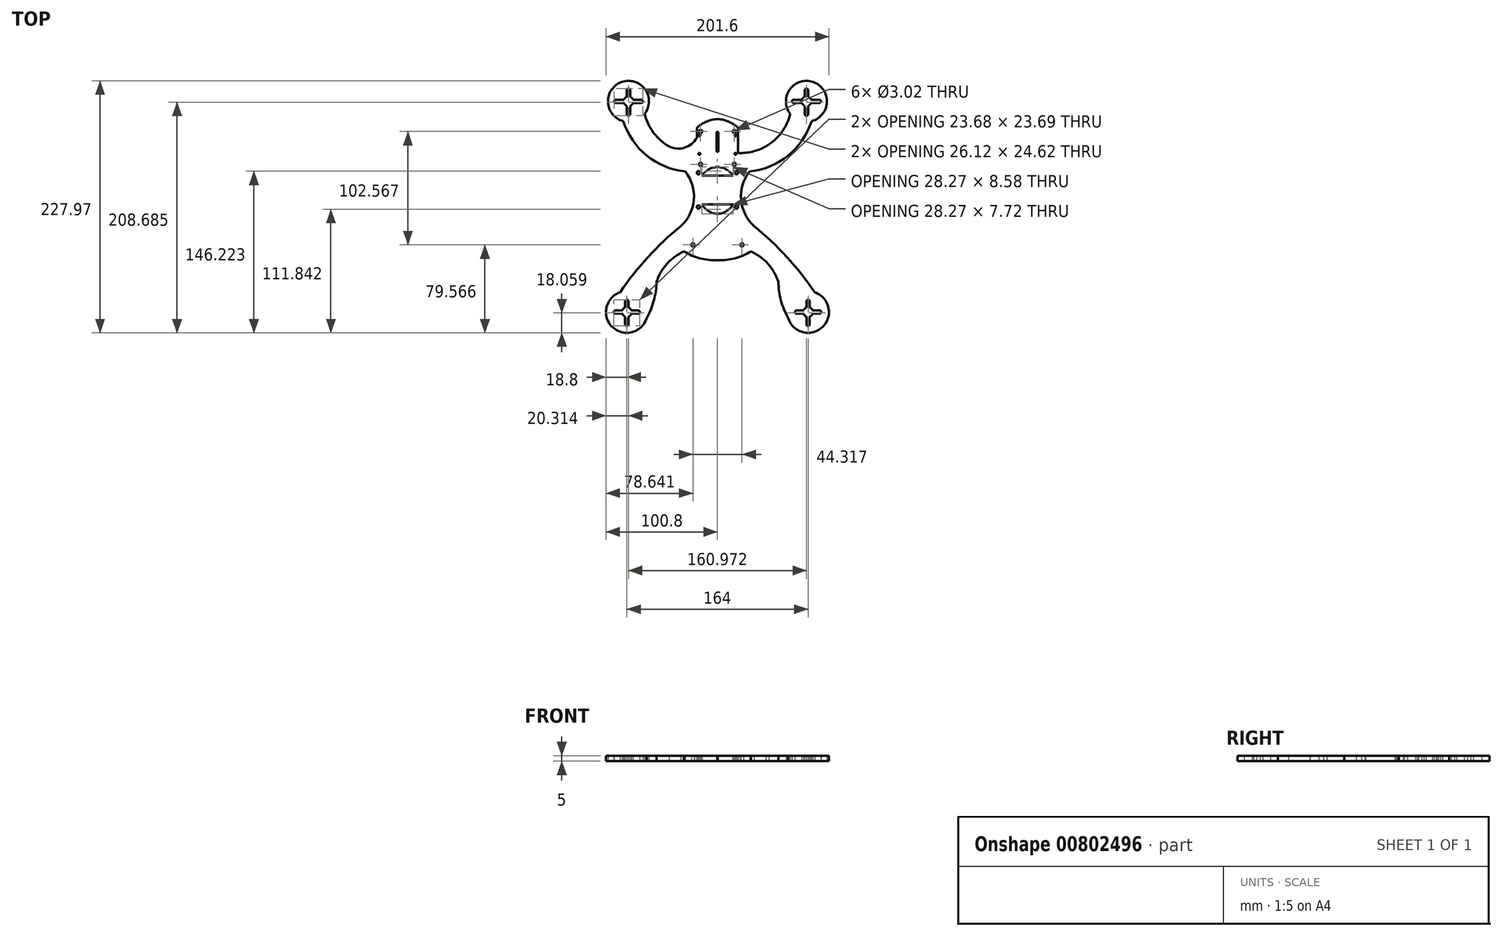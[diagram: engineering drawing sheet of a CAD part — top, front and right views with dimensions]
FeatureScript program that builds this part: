
annotation { "Feature Type Name" : "Feature", "Feature Type Description" : "" }
export const myFeature = defineFeature(function(context is Context, id is Id, definition is map)
    precondition{}
    {
        {
            var Q0;
            Q0=qCreatedBy(makeId("Top.planeOp"),FACE);
            var sketch = newSketch(context, id + "F0", { "sketchPlane" : qUnion([Q0])});
            skLineSegment(sketch, "E0", {"start": v(0, 59.62) * mm, "end": v(0, -52.38) * mm});
            skLineSegment(sketch, "E1", {"start": v(0, -52.38) * mm, "end": v(-30.19, -52.38) * mm});
            skCircle(sketch, "E2", {"center": v(-82, -107.2) * mm, "radius": 18.8 * mm});
            skCircle(sketch, "E3", {"center": v(-82, -107.2) * mm, "radius": 4.36 * mm});
            skCircle(sketch, "E4", {"center": v(-82, -118.3) * mm, "radius": 1.5 * mm});
            skCircle(sketch, "E5", {"center": v(-82, -97.6) * mm, "radius": 1.5 * mm});
            skCircle(sketch, "E6", {"center": v(-71.66, -107.2) * mm, "radius": 1.5 * mm});
            skCircle(sketch, "E7", {"center": v(-92.34, -107.2) * mm, "radius": 1.5 * mm});
            skLineSegment(sketch, "E8", {"start": v(-92.34, -108.7) * mm, "end": v(-86.1, -108.7) * mm});
            skLineSegment(sketch, "E9", {"start": v(-71.66, -108.7) * mm, "end": v(-77.9, -108.7) * mm});
            skLineSegment(sketch, "E10", {"start": v(-71.66, -105.7) * mm, "end": v(-77.9, -105.7) * mm});
            skLineSegment(sketch, "E11", {"start": v(-83.5, -118.3) * mm, "end": v(-83.5, -111.3) * mm});
            skLineSegment(sketch, "E12", {"start": v(-80.5, -118.3) * mm, "end": v(-80.5, -111.3) * mm});
            skLineSegment(sketch, "E13", {"start": v(-80.5, -97.6) * mm, "end": v(-80.5, -103.11) * mm});
            skLineSegment(sketch, "E14", {"start": v(-83.5, -97.6) * mm, "end": v(-83.5, -103.11) * mm});
            skCircle(sketch, "E15", {"center": v(-80.49, 83.43) * mm, "radius": 18.53 * mm});
            skArc(sketch, "E16", {"start": v(-64, -112.66) * mm, "mid": v(-57.49, -96.8) * mm, "end": v(-55.08, -79.81) * mm});
            skCircle(sketch, "E17", {"center": v(-80.49, 83.43) * mm, "radius": 4.36 * mm});
            skCircle(sketch, "E18", {"center": v(-80.49, 71.87) * mm, "radius": 1.5 * mm});
            skCircle(sketch, "E19", {"center": v(-68.93, 83.43) * mm, "radius": 1.5 * mm});
            skCircle(sketch, "E20", {"center": v(-92.05, 83.43) * mm, "radius": 1.5 * mm});
            skCircle(sketch, "E21", {"center": v(-80.49, 93.49) * mm, "radius": 1.5 * mm});
            skLineSegment(sketch, "E22", {"start": v(-92.05, 84.93) * mm, "end": v(-84.58, 84.93) * mm});
            skLineSegment(sketch, "E23", {"start": v(-92.05, 81.93) * mm, "end": v(-84.58, 81.93) * mm});
            skLineSegment(sketch, "E24", {"start": v(-78.99, 71.87) * mm, "end": v(-78.99, 79.33) * mm});
            skLineSegment(sketch, "E25", {"start": v(-68.93, 84.93) * mm, "end": v(-76.4, 84.93) * mm});
            skLineSegment(sketch, "E26", {"start": v(-81.99, 71.87) * mm, "end": v(-81.99, 79.33) * mm});
            skLineSegment(sketch, "E27", {"start": v(-68.93, 81.93) * mm, "end": v(-76.4, 81.93) * mm});
            skLineSegment(sketch, "E28", {"start": v(-78.99, 93.49) * mm, "end": v(-78.99, 87.52) * mm});
            skLineSegment(sketch, "E29", {"start": v(-81.99, 93.49) * mm, "end": v(-81.99, 87.52) * mm});
            skLineSegment(sketch, "E30", {"start": v(-92.34, -105.7) * mm, "end": v(-86.1, -105.7) * mm});
            skArc(sketch, "E31", {"start": v(-85.16, 65.5) * mm, "mid": v(-60.89, 32.02) * mm, "end": v(-21.44, 19.62) * mm});
            skArc(sketch, "E32", {"start": v(-20.09, -19.38) * mm, "mid": v(-57.08, -51.44) * mm, "end": v(-87.99, -89.38) * mm});
            skArc(sketch, "E33", {"start": v(-30.19, -52.38) * mm, "mid": v(-45.54, -63.46) * mm, "end": v(-55.08, -79.81) * mm});
            skArc(sketch, "E34", {"start": v(-30.19, -52.38) * mm, "mid": v(-15.7, -58.64) * mm, "end": v(0, -60.3) * mm});
            skCircle(sketch, "E35", {"center": v(-17.22, 18.8) * mm, "radius": 1.5 * mm});
            skCircle(sketch, "E36", {"center": v(-17.22, -12.2) * mm, "radius": 1.5 * mm});
            skLineSegment(sketch, "E37", {"start": v(0, 16.35) * mm, "end": v(-14.14, 16.35) * mm});
            skArc(sketch, "E38", {"start": v(0, 24.07) * mm, "mid": v(-7.95, 21.83) * mm, "end": v(-14.14, 16.35) * mm});
            skLineSegment(sketch, "E39", {"start": v(-14.14, -9.88) * mm, "end": v(0, -9.88) * mm});
            skArc(sketch, "E40", {"start": v(-14.14, -9.88) * mm, "mid": v(-8.15, -15.95) * mm, "end": v(0, -18.46) * mm});
            skCircle(sketch, "E41", {"center": v(-15.25, 26.38) * mm, "radius": 1.51 * mm});
            skCircle(sketch, "E42", {"center": v(-15.25, 56.12) * mm, "radius": 1.51 * mm});
            skLineSegment(sketch, "E43", {"start": v(-18.7, 59.62) * mm, "end": v(-18.7, 13.81) * mm});
            skArc(sketch, "E44", {"start": v(-65.76, 72.18) * mm, "mid": v(-48.67, 45.9) * mm, "end": v(-18.7, 36.71) * mm});
            skArc(sketch, "E45", {"start": v(-46.67, 44.47) * mm, "mid": v(-31.36, 41.04) * mm, "end": v(-18.7, 50.32) * mm});
            skCircle(sketch, "E46", {"center": v(-22.16, -46.44) * mm, "radius": 1.51 * mm});
            skArc(sketch, "E47", {"start": v(-33.21, -29.5) * mm, "mid": v(-21.34, -5.6) * mm, "end": v(-29.04, 19.95) * mm});
            skLineSegment(sketch, "E48", {"start": v(-21.44, 19.62) * mm, "end": v(-20.09, -19.38) * mm});
            skArc(sketch, "E49", {"start": v(0, 67.33) * mm, "mid": v(-10, 65.03) * mm, "end": v(-18.7, 59.62) * mm});
            skCircle(sketch, "E50.MirrorC", {"center": v(82, -118.3) * mm, "radius": 1.5 * mm});
            skCircle(sketch, "E51", {"center": v(-16.3, 52.75) * mm, "radius": 0.93 * mm});
            skCircle(sketch, "E52", {"center": v(0, 54.86) * mm, "radius": 0.93 * mm});
            skCircle(sketch, "E53", {"center": v(-16.3, 35.9) * mm, "radius": 0.83 * mm});
            skLineSegment(sketch, "E54", {"start": v(-17.23, 52.75) * mm, "end": v(-17.23, 35.9) * mm});
            skLineSegment(sketch, "E55", {"start": v(-15.38, 52.75) * mm, "end": v(-15.38, 35.9) * mm});
            skCircle(sketch, "E56.MirrorC", {"center": v(16.3, 52.75) * mm, "radius": 0.93 * mm});
            skLineSegment(sketch, "E57.MirrorCS", {"start": v(92.34, -105.7) * mm, "end": v(86.1, -105.7) * mm});
            skLineSegment(sketch, "E58.MirrorCS", {"start": v(80.5, -118.3) * mm, "end": v(80.5, -111.3) * mm});
            skLineSegment(sketch, "E59.MirrorCS", {"start": v(83.5, -97.6) * mm, "end": v(83.5, -103.11) * mm});
            skCircle(sketch, "E60.MirrorC", {"center": v(80.49, 83.43) * mm, "radius": 4.36 * mm});
            skLineSegment(sketch, "E61.MirrorCS", {"start": v(80.5, -97.6) * mm, "end": v(80.5, -103.11) * mm});
            skCircle(sketch, "E62.MirrorC", {"center": v(68.93, 83.43) * mm, "radius": 1.5 * mm});
            skLineSegment(sketch, "E63.MirrorCS", {"start": v(68.93, 84.93) * mm, "end": v(76.4, 84.93) * mm});
            skLineSegment(sketch, "E64.MirrorCS", {"start": v(71.66, -105.7) * mm, "end": v(77.9, -105.7) * mm});
            skLineSegment(sketch, "E65.MirrorCS", {"start": v(83.5, -118.3) * mm, "end": v(83.5, -111.3) * mm});
            skCircle(sketch, "E66.MirrorC", {"center": v(82, -97.6) * mm, "radius": 1.5 * mm});
            skCircle(sketch, "E67.MirrorC", {"center": v(82, -107.2) * mm, "radius": 4.36 * mm});
            skLineSegment(sketch, "E68.MirrorCS", {"start": v(68.93, 81.93) * mm, "end": v(76.4, 81.93) * mm});
            skCircle(sketch, "E69.MirrorC", {"center": v(16.3, 35.9) * mm, "radius": 0.83 * mm});
            skCircle(sketch, "E70.MirrorC", {"center": v(92.34, -107.2) * mm, "radius": 1.5 * mm});
            skCircle(sketch, "E71.MirrorC", {"center": v(15.25, 26.38) * mm, "radius": 1.51 * mm});
            skLineSegment(sketch, "E72.MirrorCS", {"start": v(81.99, 71.87) * mm, "end": v(81.99, 79.33) * mm});
            skCircle(sketch, "E73.MirrorC", {"center": v(15.25, 56.12) * mm, "radius": 1.51 * mm});
            skLineSegment(sketch, "E74.MirrorCS", {"start": v(92.05, 84.93) * mm, "end": v(84.58, 84.93) * mm});
            skCircle(sketch, "E75.MirrorC", {"center": v(92.05, 83.43) * mm, "radius": 1.5 * mm});
            skLineSegment(sketch, "E76.MirrorCS", {"start": v(78.99, 71.87) * mm, "end": v(78.99, 79.33) * mm});
            skLineSegment(sketch, "E77.MirrorCS", {"start": v(78.99, 93.49) * mm, "end": v(78.99, 87.52) * mm});
            skLineSegment(sketch, "E78.MirrorCS", {"start": v(81.99, 93.49) * mm, "end": v(81.99, 87.52) * mm});
            skCircle(sketch, "E79.MirrorC", {"center": v(80.49, 93.49) * mm, "radius": 1.5 * mm});
            skCircle(sketch, "E80.MirrorC", {"center": v(17.22, 18.8) * mm, "radius": 1.5 * mm});
            skCircle(sketch, "E81.MirrorC", {"center": v(80.49, 71.87) * mm, "radius": 1.5 * mm});
            skLineSegment(sketch, "E82.MirrorCS", {"start": v(92.34, -108.7) * mm, "end": v(86.1, -108.7) * mm});
            skCircle(sketch, "E83.MirrorC", {"center": v(17.22, -12.2) * mm, "radius": 1.5 * mm});
            skLineSegment(sketch, "E84.MirrorCS", {"start": v(71.66, -108.7) * mm, "end": v(77.9, -108.7) * mm});
            skLineSegment(sketch, "E85.MirrorCS", {"start": v(92.05, 81.93) * mm, "end": v(84.58, 81.93) * mm});
            skCircle(sketch, "E86.MirrorC", {"center": v(71.66, -107.2) * mm, "radius": 1.5 * mm});
            skLineSegment(sketch, "E87.MirrorCS", {"start": v(14.14, -9.88) * mm, "end": v(0, -9.88) * mm});
            skLineSegment(sketch, "E88.MirrorCS", {"start": v(17.23, 52.75) * mm, "end": v(17.23, 35.9) * mm});
            skCircle(sketch, "E89.MirrorC", {"center": v(22.16, -46.44) * mm, "radius": 1.51 * mm});
            skArc(sketch, "E90.MirrorCS", {"start": v(14.14, -9.88) * mm, "mid": v(8.15, -15.95) * mm, "end": v(0, -18.46) * mm});
            skArc(sketch, "E91.MirrorCS", {"start": v(0, 24.07) * mm, "mid": v(7.95, 21.83) * mm, "end": v(14.14, 16.35) * mm});
            skCircle(sketch, "E92.MirrorC", {"center": v(80.49, 83.43) * mm, "radius": 18.53 * mm});
            skLineSegment(sketch, "E93.MirrorCS", {"start": v(21.44, 19.62) * mm, "end": v(20.09, -19.38) * mm});
            skArc(sketch, "E94.MirrorCS", {"start": v(30.19, -52.38) * mm, "mid": v(45.54, -63.46) * mm, "end": v(55.08, -79.81) * mm});
            skArc(sketch, "E95.MirrorCS", {"start": v(0, 67.33) * mm, "mid": v(10, 65.03) * mm, "end": v(18.7, 59.62) * mm});
            skLineSegment(sketch, "E96.MirrorCS", {"start": v(0, -52.38) * mm, "end": v(30.19, -52.38) * mm});
            skArc(sketch, "E97.MirrorCS", {"start": v(65.76, 72.18) * mm, "mid": v(48.67, 45.9) * mm, "end": v(18.7, 36.71) * mm});
            skLineSegment(sketch, "E98.MirrorCS", {"start": v(15.38, 52.75) * mm, "end": v(15.38, 35.9) * mm});
            skCircle(sketch, "E99.MirrorC", {"center": v(82, -107.2) * mm, "radius": 18.8 * mm});
            skArc(sketch, "E100.MirrorCS", {"start": v(20.09, -19.38) * mm, "mid": v(57.08, -51.44) * mm, "end": v(87.99, -89.38) * mm});
            skArc(sketch, "E101.MirrorCS", {"start": v(85.16, 65.5) * mm, "mid": v(60.89, 32.02) * mm, "end": v(21.44, 19.62) * mm});
            skLineSegment(sketch, "E102.MirrorCS", {"start": v(0, 16.35) * mm, "end": v(14.14, 16.35) * mm});
            skArc(sketch, "E103.MirrorCS", {"start": v(46.67, 44.47) * mm, "mid": v(31.36, 41.04) * mm, "end": v(18.7, 50.32) * mm});
            skLineSegment(sketch, "E104.MirrorCS", {"start": v(18.7, 59.62) * mm, "end": v(18.7, 13.81) * mm});
            skArc(sketch, "E105.MirrorCS", {"start": v(30.19, -52.38) * mm, "mid": v(15.7, -58.64) * mm, "end": v(0, -60.3) * mm});
            skArc(sketch, "E106.MirrorCS", {"start": v(64, -112.66) * mm, "mid": v(57.49, -96.8) * mm, "end": v(55.08, -79.81) * mm});
            skArc(sketch, "E107.MirrorCS", {"start": v(33.21, -29.5) * mm, "mid": v(21.34, -5.6) * mm, "end": v(29.04, 19.95) * mm});
            skLineSegment(sketch, "E108", {"start": v(0, 54.86) * mm, "end": v(0, 39.75) * mm});
            skCircle(sketch, "E109", {"center": v(0, 38.7) * mm, "radius": 0.93 * mm});
            skLineSegment(sketch, "E110", {"start": v(-0.93, 54.86) * mm, "end": v(-0.93, 38.7) * mm});
            skLineSegment(sketch, "E111", {"start": v(0.93, 54.86) * mm, "end": v(0.93, 38.7) * mm});
            skSolve(sketch);
        }
        {
            var Q0;
            Q0=makeQuery(id+"F0.imprint","IMPRINT",FACE,{"disambiguationData":[TD([[makeQuery(id+"F0.imprint","IMPRINT",EDGE,{"derivedFrom":sQuery(id+"F0.wireOp",EDGE,"E1")}),1.0]])]});
            var Q1;
            {var subQ2=sQuery(id+"F0.wireOp",EDGE,"E47");Q1=makeQuery(id+"F0.imprint","IMPRINT",FACE,{"disambiguationData":[TD([[makeQuery(id+"F0.imprint","IMPRINT",EDGE,{"derivedFrom":subQ2}),-1.0]])]});}
            var Q2;
            {var subQ0=sQuery(id+"F0.wireOp",EDGE,"E44");var subQ1=sQuery(id+"F0.wireOp",EDGE,"E43");var subQ2=makeQuery(id+"F0.imprint","INTERSECT",VERTEX,{"derivedFrom":[subQ1,subQ0]});Q2=makeQuery(id+"F0.imprint","IMPRINT",FACE,{"disambiguationData":[TD([[makeQuery(id+"F0.imprint","IMPRINT",EDGE,{"disambiguationData":[TD([[subQ2,1.0]])],"derivedFrom":subQ1}),-1.0]])]});}
            var Q3;
            {var subQ0=sQuery(id+"F0.wireOp",EDGE,"E45");var subQ1=sQuery(id+"F0.wireOp",EDGE,"E44");var subQ2=makeQuery(id+"F0.imprint","INTERSECT",VERTEX,{"disambiguationData":[OD(0.0)],"derivedFrom":[subQ1,subQ0]});Q3=makeQuery(id+"F0.imprint","IMPRINT",FACE,{"disambiguationData":[TD([[makeQuery(id+"F0.imprint","IMPRINT",EDGE,{"disambiguationData":[TD([[subQ2,-1.0]])],"derivedFrom":subQ1}),-1.0]])]});}
            var Q4;
            Q4=makeQuery(id+"F0.imprint","IMPRINT",FACE,{"disambiguationData":[TD([[makeQuery(id+"F0.imprint","IMPRINT",EDGE,{"derivedFrom":sQuery(id+"F0.wireOp",EDGE,"1970e8cf-01bf-4d2f-893a-c7edce89ae3a28.MirrorC")}),-1.0]])]});
            var Q5;
            {var subQ0=sQuery(id+"F0.wireOp",EDGE,"1970e8cf-01bf-4d2f-893a-c7edce89ae3a36.MirrorCS");Q5=makeQuery(id+"F0.imprint","IMPRINT",FACE,{"disambiguationData":[TD([[makeQuery(id+"F0.imprint","IMPRINT",EDGE,{"derivedFrom":subQ0}),1.0]])]});}
            var Q6;
            {var subQ0=sQuery(id+"F0.wireOp",EDGE,"1970e8cf-01bf-4d2f-893a-c7edce89ae3a47.MirrorCS");var subQ1=sQuery(id+"F0.wireOp",EDGE,"1970e8cf-01bf-4d2f-893a-c7edce89ae3a38.MirrorCS");var subQ2=makeQuery(id+"F0.imprint","INTERSECT",VERTEX,{"disambiguationData":[OD(0.0)],"derivedFrom":[subQ1,subQ0]});Q6=makeQuery(id+"F0.imprint","IMPRINT",FACE,{"disambiguationData":[TD([[makeQuery(id+"F0.imprint","IMPRINT",EDGE,{"disambiguationData":[TD([[subQ2,-1.0]])],"derivedFrom":subQ1}),1.0]])]});}
            var Q7;
            {var subQ0=sQuery(id+"F0.wireOp",EDGE,"1970e8cf-01bf-4d2f-893a-c7edce89ae3a46.MirrorCS");var subQ1=sQuery(id+"F0.wireOp",EDGE,"1970e8cf-01bf-4d2f-893a-c7edce89ae3a38.MirrorCS");var subQ2=makeQuery(id+"F0.imprint","INTERSECT",VERTEX,{"derivedFrom":[subQ1,subQ0]});Q7=makeQuery(id+"F0.imprint","IMPRINT",FACE,{"disambiguationData":[TD([[makeQuery(id+"F0.imprint","IMPRINT",EDGE,{"disambiguationData":[TD([[subQ2,1.0]])],"derivedFrom":subQ1}),-1.0]])]});}
            var Q8;
            {var subQ2=sQuery(id+"F0.wireOp",EDGE,"1970e8cf-01bf-4d2f-893a-c7edce89ae3a24.MirrorCS");Q8=makeQuery(id+"F0.imprint","IMPRINT",FACE,{"disambiguationData":[TD([[makeQuery(id+"F0.imprint","IMPRINT",EDGE,{"derivedFrom":subQ2}),-1.0]])]});}
            var Q9;
            {var subQ0=sQuery(id+"F0.wireOp",EDGE,"E43");var subQ1=sQuery(id+"F0.wireOp",EDGE,"E35");var subQ2=makeQuery(id+"F0.imprint","INTERSECT",VERTEX,{"disambiguationData":[OD(0.0)],"derivedFrom":[subQ1,subQ0]});Q9=makeQuery(id+"F0.imprint","IMPRINT",FACE,{"disambiguationData":[TD([[makeQuery(id+"F0.imprint","IMPRINT",EDGE,{"disambiguationData":[TD([[subQ2,1.0]])],"derivedFrom":subQ1}),1.0]])]});}
            var Q10;
            {var subQ0=sQuery(id+"F0.wireOp",EDGE,"1970e8cf-01bf-4d2f-893a-c7edce89ae3a46.MirrorCS");var subQ1=sQuery(id+"F0.wireOp",EDGE,"1970e8cf-01bf-4d2f-893a-c7edce89ae3a11.MirrorC");var subQ2=makeQuery(id+"F0.imprint","INTERSECT",VERTEX,{"disambiguationData":[OD(0.0)],"derivedFrom":[subQ1,subQ0]});Q10=makeQuery(id+"F0.imprint","IMPRINT",FACE,{"disambiguationData":[TD([[makeQuery(id+"F0.imprint","IMPRINT",EDGE,{"disambiguationData":[TD([[subQ2,1.0]])],"derivedFrom":subQ1}),-1.0]])]});}
            var Q11;
            {var subQ0=sQuery(id+"F0.wireOp",EDGE,"E8");Q11=makeQuery(id+"F0.imprint","IMPRINT",FACE,{"disambiguationData":[TD([[makeQuery(id+"F0.imprint","IMPRINT",EDGE,{"derivedFrom":subQ0}),-1.0]])]});}
            var Q12;
            {var subQ3=sQuery(id+"F0.wireOp",EDGE,"E22");Q12=makeQuery(id+"F0.imprint","IMPRINT",FACE,{"disambiguationData":[TD([[makeQuery(id+"F0.imprint","IMPRINT",EDGE,{"derivedFrom":subQ3}),1.0]])]});}
            var Q13;
            {var subQ13=sQuery(id+"F0.wireOp",EDGE,"1970e8cf-01bf-4d2f-893a-c7edce89ae3a8.MirrorCS");Q13=makeQuery(id+"F0.imprint","IMPRINT",FACE,{"disambiguationData":[TD([[makeQuery(id+"F0.imprint","IMPRINT",EDGE,{"derivedFrom":subQ13}),1.0]])]});}
            var Q14;
            {var subQ2=sQuery(id+"F0.wireOp",EDGE,"1970e8cf-01bf-4d2f-893a-c7edce89ae3a1.MirrorCS");Q14=makeQuery(id+"F0.imprint","IMPRINT",FACE,{"disambiguationData":[TD([[makeQuery(id+"F0.imprint","IMPRINT",EDGE,{"derivedFrom":subQ2}),-1.0]])]});}
            var Q15;
            {var subQ1=sQuery(id+"F0.wireOp",EDGE,"71e4ceb2-40d3-4ac1-b8c6-fa41186b85900.MirrorCS");Q15=makeQuery(id+"F0.imprint","IMPRINT",FACE,{"disambiguationData":[TD([[makeQuery(id+"F0.imprint","IMPRINT",EDGE,{"derivedFrom":subQ1}),1.0]])]});}
            var Q16;
            {var subQ3=sQuery(id+"F0.wireOp",EDGE,"71e4ceb2-40d3-4ac1-b8c6-fa41186b85902.MirrorCS");Q16=makeQuery(id+"F0.imprint","IMPRINT",FACE,{"disambiguationData":[TD([[makeQuery(id+"F0.imprint","IMPRINT",EDGE,{"derivedFrom":subQ3}),-1.0]])]});}
            var Q17;
            {var subQ0=sQuery(id+"F0.wireOp",EDGE,"71e4ceb2-40d3-4ac1-b8c6-fa41186b859038.MirrorCS");var subQ1=sQuery(id+"F0.wireOp",EDGE,"71e4ceb2-40d3-4ac1-b8c6-fa41186b859036.MirrorCS");var subQ2=makeQuery(id+"F0.imprint","INTERSECT",VERTEX,{"derivedFrom":[subQ1,subQ0]});Q17=makeQuery(id+"F0.imprint","IMPRINT",FACE,{"disambiguationData":[TD([[makeQuery(id+"F0.imprint","IMPRINT",EDGE,{"disambiguationData":[TD([[subQ2,-1.0]])],"derivedFrom":subQ1}),1.0]])]});}
            var Q18;
            {var subQ0=sQuery(id+"F0.wireOp",EDGE,"71e4ceb2-40d3-4ac1-b8c6-fa41186b859045.MirrorCS");Q18=makeQuery(id+"F0.imprint","IMPRINT",FACE,{"disambiguationData":[TD([[makeQuery(id+"F0.imprint","IMPRINT",EDGE,{"derivedFrom":subQ0}),1.0]])]});}
            var Q19;
            {var subQ3=sQuery(id+"F0.wireOp",EDGE,"E63.MirrorCS");Q19=makeQuery(id+"F0.imprint","IMPRINT",FACE,{"disambiguationData":[TD([[makeQuery(id+"F0.imprint","IMPRINT",EDGE,{"derivedFrom":subQ3}),1.0]])]});}
            var Q20;
            {var subQ8=sQuery(id+"F0.wireOp",EDGE,"E57.MirrorCS");Q20=makeQuery(id+"F0.imprint","IMPRINT",FACE,{"disambiguationData":[TD([[makeQuery(id+"F0.imprint","IMPRINT",EDGE,{"derivedFrom":subQ8}),-1.0]])]});}
            var Q21;
            Q21=makeQuery(id+"F0.imprint","IMPRINT",FACE,{"disambiguationData":[TD([[makeQuery(id+"F0.imprint","IMPRINT",EDGE,{"derivedFrom":sQuery(id+"F0.wireOp",EDGE,"E1")}),-1.0]])]});
            var Q22;
            {var subQ0=sQuery(id+"F0.wireOp",EDGE,"E104.MirrorCS");var subQ1=sQuery(id+"F0.wireOp",EDGE,"E97.MirrorCS");var subQ2=makeQuery(id+"F0.imprint","INTERSECT",VERTEX,{"derivedFrom":[subQ1,subQ0]});Q22=makeQuery(id+"F0.imprint","IMPRINT",FACE,{"disambiguationData":[TD([[makeQuery(id+"F0.imprint","IMPRINT",EDGE,{"disambiguationData":[TD([[subQ2,1.0]])],"derivedFrom":subQ1}),-1.0]])]});}
            var Q23;
            {var subQ0=sQuery(id+"F0.wireOp",EDGE,"E93.MirrorCS");Q23=makeQuery(id+"F0.imprint","IMPRINT",FACE,{"disambiguationData":[TD([[makeQuery(id+"F0.imprint","IMPRINT",EDGE,{"derivedFrom":subQ0}),1.0]])]});}
            extrude(context, id + "F1", {"entities" : qUnion([Q0, Q1, Q2, Q3, Q4, Q5, Q6, Q7, Q8, Q9, Q10, Q11, Q12, Q13, Q14, Q15, Q16, Q17, Q18, Q19, Q20, Q21, Q22, Q23]), "endBound" : BoundingType.SYMMETRIC, "depth" : 5 * mm, "offsetDistance" : 25 * mm});
        }
    });
